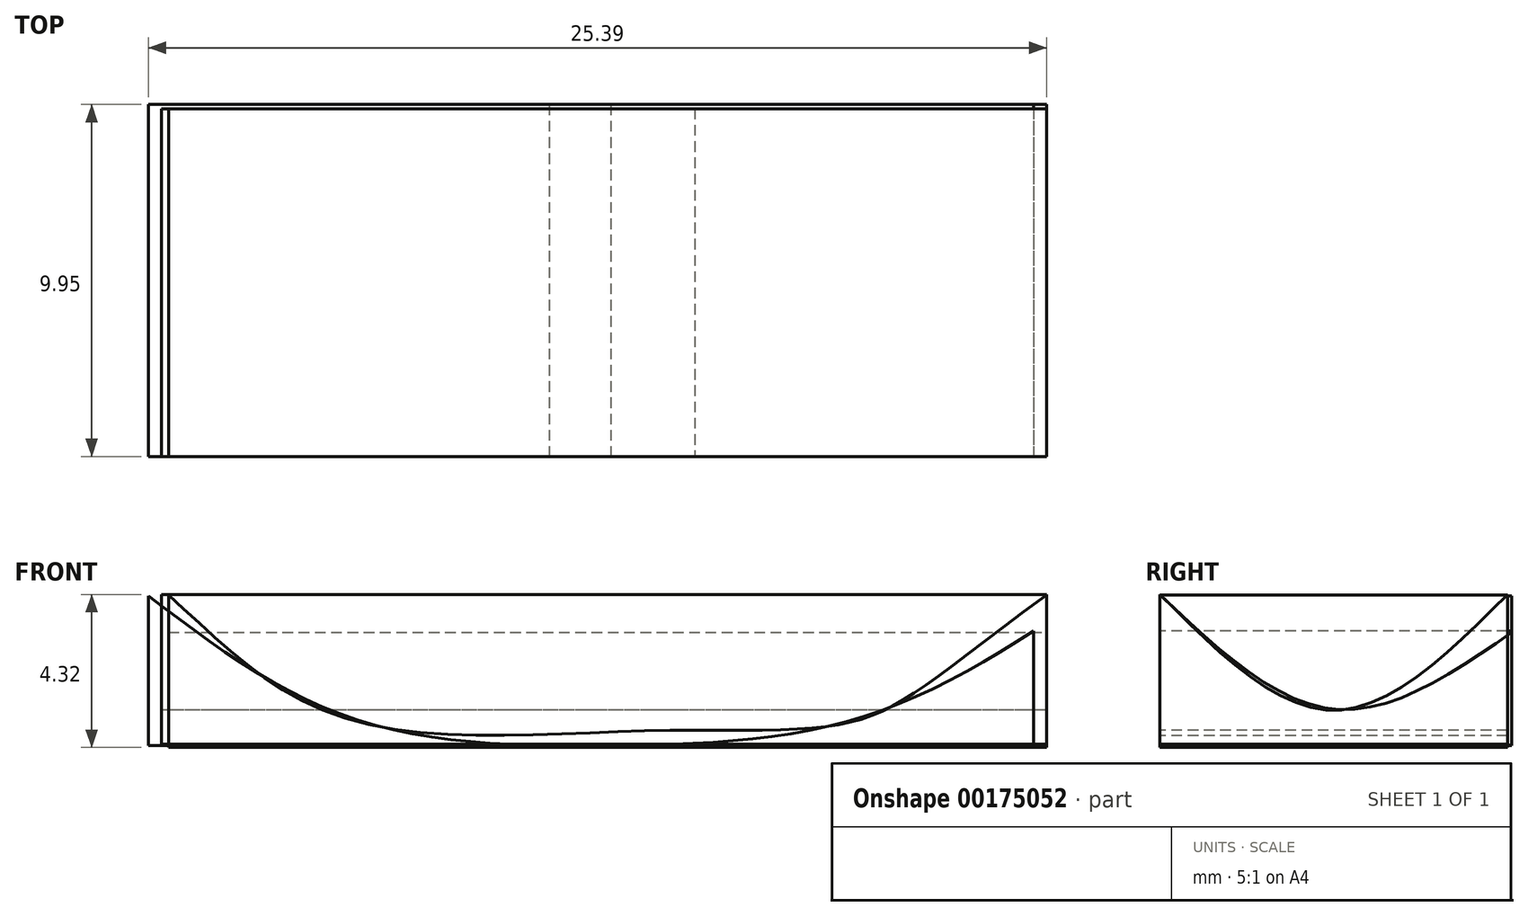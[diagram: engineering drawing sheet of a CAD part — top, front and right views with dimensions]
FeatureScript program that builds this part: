
annotation { "Feature Type Name" : "Feature", "Feature Type Description" : "" }
export const myFeature = defineFeature(function(context is Context, id is Id, definition is map)
    precondition{}
    {
        {
            var Q0;
            Q0=qCreatedBy(makeId("Front.planeOp"),FACE);
            var sketch = newSketch(context, id + "F0", { "sketchPlane" : qUnion([Q0])});
            skLineSegment(sketch, "E0", {"start": v(-25.39, 2.79) * mm, "end": v(-0.37, 2.79) * mm});
            skLineSegment(sketch, "E1", {"start": v(-25.39, 7.02) * mm, "end": v(-25.39, 2.79) * mm});
            skLineSegment(sketch, "E2", {"start": v(-0.37, 7.02) * mm, "end": v(-0.37, 2.79) * mm});
            skFitSpline(sketch, "E3", {"points": [v(-25.39, 7.02) * mm, v(-19.56, 3.54) * mm, v(-12.32, 2.79) * mm, v(-5.8, 3.43) * mm, v(-0.37, 6.03) * mm], "startDerivative": vector(21.81, -16.58) * mm, "endDerivative": vector(22.53, 14.68) * mm});
            skSolve(sketch);
        }
        {
            var Q0;
            Q0=qCreatedBy(makeId("Right.planeOp"),FACE);
            var sketch = newSketch(context, id + "F1", { "sketchPlane" : qUnion([Q0])});
            skLineSegment(sketch, "E4", {"start": v(0, 2.8) * mm, "end": v(9.95, 2.8) * mm});
            skLineSegment(sketch, "E5", {"start": v(9.95, 7.05) * mm, "end": v(9.95, 2.8) * mm});
            skFitSpline(sketch, "E6", {"points": [v(0, 7.05) * mm, v(4.97, 3.81) * mm, v(9.95, 5.98) * mm], "startDerivative": vector(9.62, -9.1) * mm, "endDerivative": vector(10.28, 7.08) * mm});
            skLineSegment(sketch, "E7", {"start": v(0, 7.05) * mm, "end": v(0, 2.8) * mm});
            skSolve(sketch);
        }
        {
            var Q0;
            Q0=qCreatedBy(makeId("Front.planeOp"),FACE);
            var sketch = newSketch(context, id + "F2", { "sketchPlane" : qUnion([Q0])});
            skLineSegment(sketch, "E8", {"start": v(0, 7.05) * mm, "end": v(0, 2.74) * mm});
            skLineSegment(sketch, "E9", {"start": v(0, 2.74) * mm, "end": v(-24.82, 2.74) * mm});
            skLineSegment(sketch, "E10", {"start": v(-24.82, 2.74) * mm, "end": v(-24.82, 7.05) * mm});
            skFitSpline(sketch, "E11", {"points": [v(-24.82, 7.05) * mm, v(-19.68, 3.52) * mm, v(-9.95, 3.22) * mm], "startDerivative": vector(9.91, -8.95) * mm, "endDerivative": vector(15.32, -0.31) * mm});
            skFitSpline(sketch, "E12", {"points": [v(-9.95, 3.22) * mm, v(0, 7.05) * mm], "startDerivative": vector(17.03, -0.03) * mm, "endDerivative": vector(15.63, 11.48) * mm});
            skSolve(sketch);
        }
        {
            var Q0;
            Q0=qCreatedBy(makeId("Right.planeOp"),FACE);
            var sketch = newSketch(context, id + "F3", { "sketchPlane" : qUnion([Q0])});
            skLineSegment(sketch, "E13", {"start": v(9.83, 7.06) * mm, "end": v(9.83, 2.82) * mm});
            skLineSegment(sketch, "E14", {"start": v(9.83, 2.82) * mm, "end": v(0, 2.82) * mm});
            skLineSegment(sketch, "E15", {"start": v(0, 2.82) * mm, "end": v(0, 7.06) * mm});
            skFitSpline(sketch, "E16", {"points": [v(9.83, 7.06) * mm, v(4.91, 3.79) * mm, v(0, 7.06) * mm], "startDerivative": vector(-9.83, -9.83) * mm, "endDerivative": vector(-9.83, 9.83) * mm});
            skSolve(sketch);
        }
        {
            var Q0;
            {var subQ0=sQuery(id+"F0.wireOp",EDGE,"E1");Q0=makeQuery(id+"F0.imprint","IMPRINT",FACE,{"disambiguationData":[TD([[makeQuery(id+"F0.imprint","IMPRINT",EDGE,{"derivedFrom":subQ0}),1.0]])]});}
            var Q1;
            {var subQ0=sQuery(id+"F0.wireOp",EDGE,"E0");var subQ1=sQuery(id+"F0.wireOp",EDGE,"E2");var subQ2=makeQuery(id+"F0.imprint","INTERSECT",VERTEX,{"derivedFrom":[subQ1,subQ0]});Q1=makeQuery(id+"F0.imprint","IMPRINT",FACE,{"disambiguationData":[TD([[makeQuery(id+"F0.imprint","IMPRINT",EDGE,{"disambiguationData":[TD([[subQ2,1.0]])],"derivedFrom":subQ1}),-1.0]])]});}
            extrude(context, id + "F4", {"entities" : qUnion([Q0, Q1]), "oppositeDirection" : true, "depth" : 9.95 * mm});
        }
        {
            var Q0;
            {var subQ0=sQuery(id+"F1.wireOp",EDGE,"E4");Q0=makeQuery(id+"F1.imprint","IMPRINT",FACE,{"disambiguationData":[TD([[makeQuery(id+"F1.imprint","IMPRINT",EDGE,{"derivedFrom":subQ0}),1.0]])]});}
            extrude(context, id + "F5", {"entities" : qUnion([Q0]), "oppositeDirection" : true, "depth" : 24.82 * mm});
        }
        {
            var Q0;
            Q0=makeQuery(id+"F2.imprint","IMPRINT",FACE,{"disambiguationData":[TD([[makeQuery(id+"F2.imprint","IMPRINT",EDGE,{"derivedFrom":sQuery(id+"F2.wireOp",EDGE,"E8")}),-1.0]])]});
            extrude(context, id + "F6", {"entities" : qUnion([Q0]), "oppositeDirection" : true, "depth" : 9.83 * mm});
        }
        {
            var Q0;
            Q0=makeQuery(id+"F3.imprint","IMPRINT",FACE,{"disambiguationData":[TD([[makeQuery(id+"F3.imprint","IMPRINT",EDGE,{"derivedFrom":sQuery(id+"F3.wireOp",EDGE,"E13")}),-1.0]])]});
            extrude(context, id + "F7", {"entities" : qUnion([Q0]), "oppositeDirection" : true, "depth" : 25.01 * mm});
        }
    });
